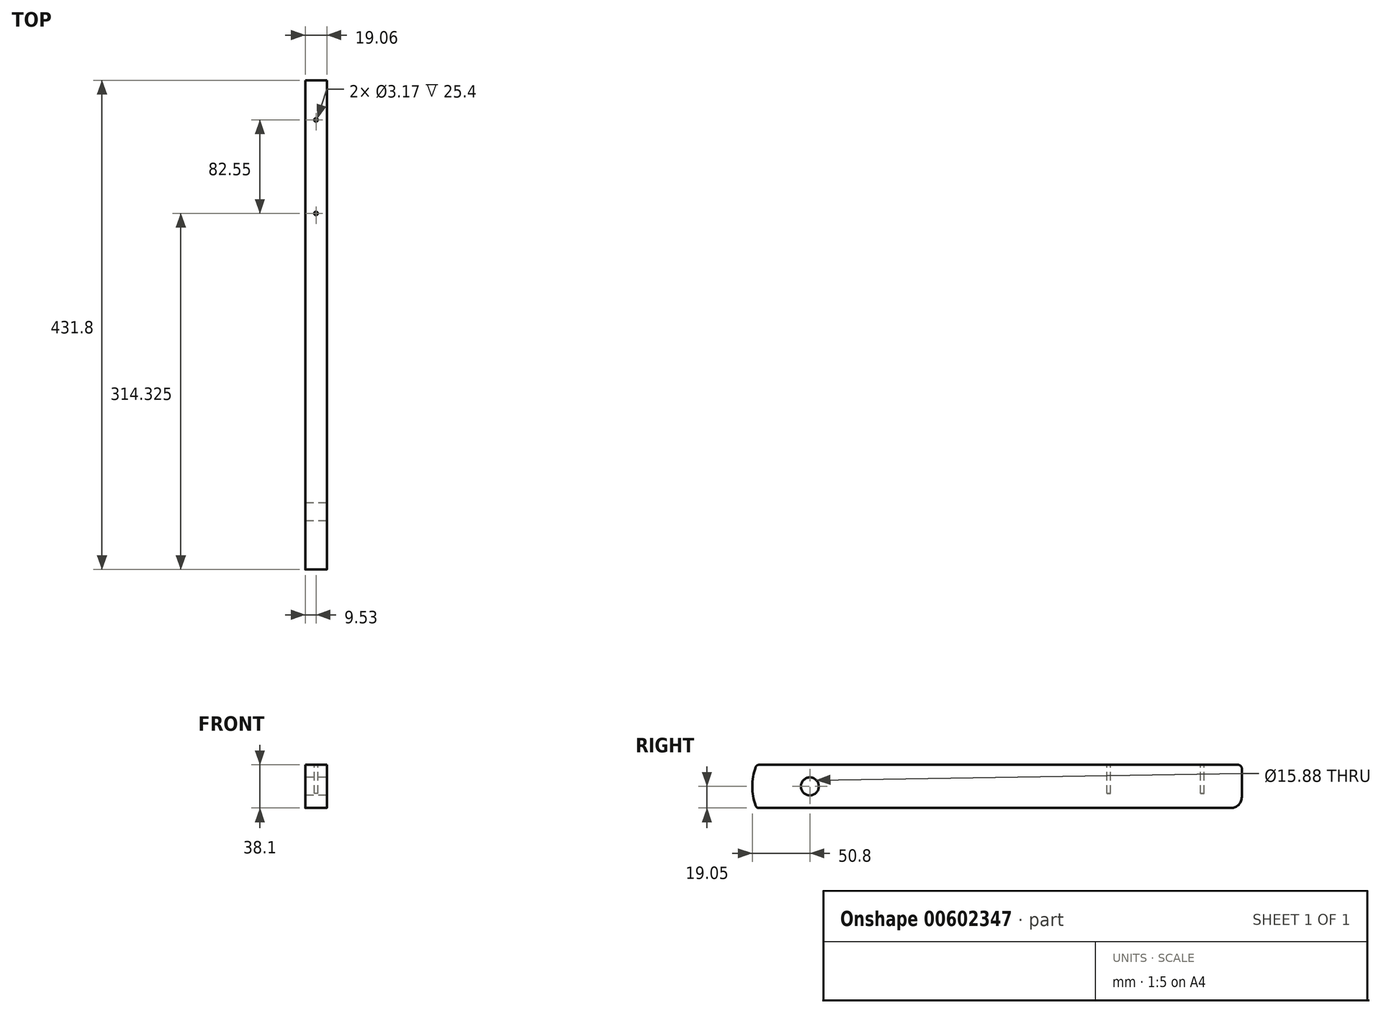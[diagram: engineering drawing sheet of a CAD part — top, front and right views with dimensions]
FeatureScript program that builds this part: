
annotation { "Feature Type Name" : "Feature", "Feature Type Description" : "" }
export const myFeature = defineFeature(function(context is Context, id is Id, definition is map)
    precondition{}
    {
        {
            var Q0;
            Q0=qCreatedBy(makeId("Right.planeOp"),FACE);
            var sketch = newSketch(context, id + "F0", { "sketchPlane" : qUnion([Q0])});
            skLineSegment(sketch, "E0.bottom", {"start": v(381, 19.05) * mm, "end": v(-47.1, 19.05) * mm});
            skLineSegment(sketch, "E0.top", {"start": v(381, -19.05) * mm, "end": v(-47.1, -19.05) * mm});
            skLineSegment(sketch, "E0.right", {"start": v(-50.8, 19.05) * mm, "end": v(-50.8, -19.05) * mm, "construction": true});
            skPoint(sketch, "E0.middle", {"position": v(0, 0) * mm});
            skCircle(sketch, "E1", {"center": v(0, 0) * mm, "radius": 7.94 * mm});
            skLineSegment(sketch, "E2", {"start": v(0, 0) * mm, "end": v(-50.8, 0) * mm, "construction": true});
            skArc(sketch, "E3", {"start": v(-47.1, 19.05) * mm, "mid": v(-50.8, 0) * mm, "end": v(-47.1, -19.05) * mm});
            skLineSegment(sketch, "E4", {"start": v(-50.8, 19.05) * mm, "end": v(-47.1, 19.05) * mm, "construction": true});
            skLineSegment(sketch, "E5", {"start": v(-47.1, -19.05) * mm, "end": v(-50.8, -19.05) * mm, "construction": true});
            skLineSegment(sketch, "E6", {"start": v(381, 19.05) * mm, "end": v(381, -19.05) * mm});
            skLineSegment(sketch, "E7", {"start": v(304.8, 19.05) * mm, "end": v(304.8, -19.05) * mm, "construction": true});
            skSolve(sketch);
        }
        {
            var Q0;
            Q0 = qSketchRegion(id + "F0", true);
            extrude(context, id + "F1", {"entities" : qUnion([Q0]), "endBound" : BoundingType.SYMMETRIC, "depth" : 19.05 * mm, "offsetDistance" : 25.4 * mm});
        }
        {
            var Q0;
            Q0=makeQuery(id+"F1.opExtrude","SWEPT_FACE",FACE,{"disambiguationData":[OSD([sQuery(id+"F0.wireOp",EDGE,"E0.bottom")])]});
            var sketch = newSketch(context, id + "F2", { "sketchPlane" : qUnion([Q0])});
            skLineSegment(sketch, "E8", {"start": v(-9.53, 304.8) * mm, "end": v(9.53, 304.8) * mm, "construction": true});
            skLineSegment(sketch, "E9", {"start": v(0, 346.08) * mm, "end": v(0, 304.8) * mm, "construction": true});
            skLineSegment(sketch, "E10", {"start": v(0, 304.8) * mm, "end": v(0, 263.53) * mm, "construction": true});
            skCircle(sketch, "E11", {"center": v(0, 346.08) * mm, "radius": 1.59 * mm});
            skCircle(sketch, "E12", {"center": v(0, 263.53) * mm, "radius": 1.59 * mm});
            skSolve(sketch);
        }
        {
            var Q0;
            Q0 = qSketchRegion(id + "F2", true);
            extrude(context, id + "F3", {"entities" : qUnion([Q0]), "operationType" : NewBodyOperationType.REMOVE, "oppositeDirection" : true, "depth" : 25.4 * mm, "offsetDistance" : 25.4 * mm});
        }
        {
            var Q0;
            Q0=makeQuery(id+"F1.opExtrude","SWEPT_EDGE",EDGE,{"disambiguationData":[OSD([sQuery(id+"F0.wireOp",EDGE,"E0.top"),sQuery(id+"F0.wireOp",EDGE,"E6")])]});
            fillet(context, id + "F4", {"entities" : qUnion([Q0]), "radius" : 9.52 * mm, "tangentPropagation" : true, "allowEdgeOverflow" : false});
        }
        {
            var Q0;
            Q0=makeQuery(id+"F1.opExtrude","SWEPT_EDGE",EDGE,{"disambiguationData":[OSD([sQuery(id+"F0.wireOp",EDGE,"E0.bottom"),sQuery(id+"F0.wireOp",EDGE,"E6")])]});
            var Q1;
            Q1=makeQuery(id+"F1.opExtrude","SWEPT_EDGE",EDGE,{"disambiguationData":[OSD([sQuery(id+"F0.wireOp",EDGE,"E0.top"),sQuery(id+"F0.wireOp",EDGE,"E3")])]});
            var Q2;
            Q2=makeQuery(id+"F1.opExtrude","SWEPT_EDGE",EDGE,{"disambiguationData":[OSD([sQuery(id+"F0.wireOp",EDGE,"E0.bottom"),sQuery(id+"F0.wireOp",EDGE,"E3")])]});
            fillet(context, id + "F5", {"entities" : qUnion([Q0, Q1, Q2]), "radius" : 3.17 * mm, "tangentPropagation" : true, "allowEdgeOverflow" : false});
        }
    });
